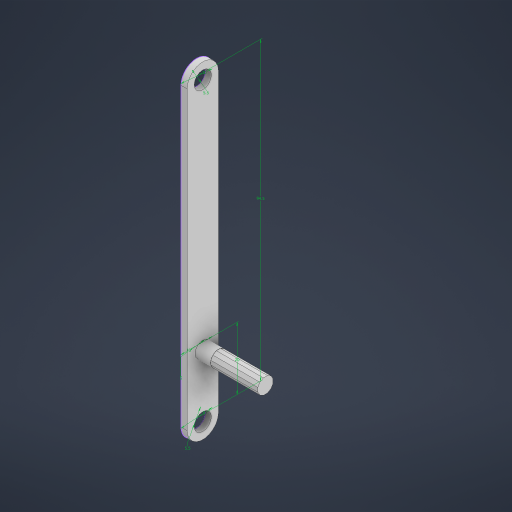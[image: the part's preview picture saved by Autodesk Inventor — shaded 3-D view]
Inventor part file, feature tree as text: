
AUTODESK INVENTOR PART (.ipt)
format: ipt  version: 2024.1 (Build 281209000, 209)  size: 496,128 bytes
history: native  units: mm
features: extrude x3, other x1, sketch x1
ambient origin geometry x8: Origin, YZ Plane, XZ Plane, XY Plane, X Axis, Y Axis, Z Axis, Center Point
bodies: Body1 (feature_tree)
feature tree (5):
  other  "솔리드1"
  sketch  "스케치1"
  extrude  "돌출1"  Depth=5.0mm
  extrude  "돌출2"  Depth=10.0mm
  extrude  "돌출3"  Depth=10.0mm
